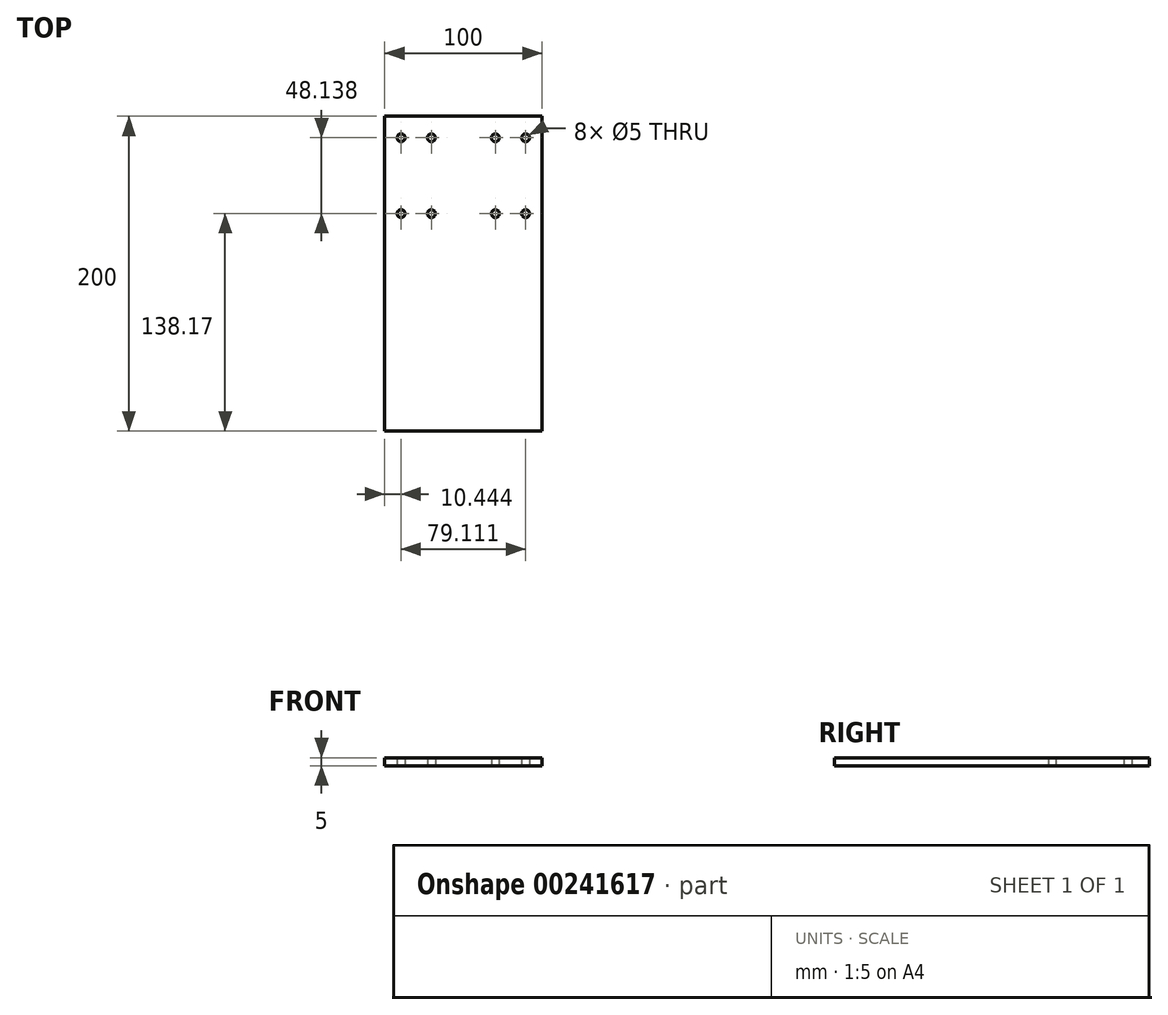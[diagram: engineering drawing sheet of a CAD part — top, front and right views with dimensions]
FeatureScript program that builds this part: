
annotation { "Feature Type Name" : "Feature", "Feature Type Description" : "" }
export const myFeature = defineFeature(function(context is Context, id is Id, definition is map)
    precondition{}
    {
        {
            var Q0;
            Q0=qCreatedBy(makeId("Top.planeOp"),FACE);
            var sketch = newSketch(context, id + "F0", { "sketchPlane" : qUnion([Q0])});
            skLineSegment(sketch, "E0.bottom", {"start": v(0, 0) * mm, "end": v(100, 0) * mm});
            skLineSegment(sketch, "E0.top", {"start": v(0, 200) * mm, "end": v(100, 200) * mm});
            skLineSegment(sketch, "E0.left", {"start": v(0, 0) * mm, "end": v(0, 200) * mm});
            skLineSegment(sketch, "E0.right", {"start": v(100, 0) * mm, "end": v(100, 200) * mm});
            skLineSegment(sketch, "E1", {"start": v(50, 200) * mm, "end": v(50, 0) * mm});
            skLineSegment(sketch, "E2.bottom", {"start": v(10.44, 186.3) * mm, "end": v(29.7, 186.3) * mm});
            skLineSegment(sketch, "E2.top", {"start": v(10.44, 138.17) * mm, "end": v(29.7, 138.17) * mm});
            skLineSegment(sketch, "E2.left", {"start": v(10.44, 186.3) * mm, "end": v(10.44, 138.17) * mm});
            skLineSegment(sketch, "E2.right", {"start": v(29.7, 186.3) * mm, "end": v(29.7, 138.17) * mm});
            skLineSegment(sketch, "E3.MirrorCS", {"start": v(89.56, 138.17) * mm, "end": v(70.3, 138.17) * mm});
            skLineSegment(sketch, "E4.MirrorCS", {"start": v(89.56, 186.3) * mm, "end": v(70.3, 186.3) * mm});
            skLineSegment(sketch, "E5.MirrorCS", {"start": v(70.3, 186.3) * mm, "end": v(70.3, 138.17) * mm});
            skLineSegment(sketch, "E6.MirrorCS", {"start": v(89.56, 186.3) * mm, "end": v(89.56, 138.17) * mm});
            skCircle(sketch, "E7", {"center": v(10.44, 186.3) * mm, "radius": 2.5 * mm});
            skCircle(sketch, "E8", {"center": v(29.7, 186.3) * mm, "radius": 2.5 * mm});
            skCircle(sketch, "E9", {"center": v(29.7, 138.17) * mm, "radius": 2.5 * mm});
            skCircle(sketch, "E10", {"center": v(10.44, 138.17) * mm, "radius": 2.5 * mm});
            skCircle(sketch, "E11", {"center": v(70.3, 186.3) * mm, "radius": 2.5 * mm});
            skCircle(sketch, "E12", {"center": v(89.56, 186.3) * mm, "radius": 2.5 * mm});
            skCircle(sketch, "E13", {"center": v(70.3, 138.17) * mm, "radius": 2.5 * mm});
            skCircle(sketch, "E14", {"center": v(89.56, 138.17) * mm, "radius": 2.5 * mm});
            skSolve(sketch);
        }
        {
            var Q0;
            {var subQ11=sQuery(id+"F0.wireOp",EDGE,"E0.right");Q0=makeQuery(id+"F0.imprint","IMPRINT",FACE,{"disambiguationData":[TD([[makeQuery(id+"F0.imprint","IMPRINT",EDGE,{"derivedFrom":subQ11}),1.0]])]});}
            var Q1;
            {var subQ10=sQuery(id+"F0.wireOp",EDGE,"E7");var subQ13=sQuery(id+"F0.wireOp",EDGE,"E2.bottom");var subQ14=makeQuery(id+"F0.imprint","INTERSECT",VERTEX,{"derivedFrom":[subQ13,subQ10]});Q1=makeQuery(id+"F0.imprint","IMPRINT",FACE,{"disambiguationData":[TD([[makeQuery(id+"F0.imprint","IMPRINT",EDGE,{"disambiguationData":[TD([[subQ14,-1.0]])],"derivedFrom":subQ13}),-1.0]])]});}
            var Q2;
            {var subQ15=sQuery(id+"F0.wireOp",EDGE,"E0.left");Q2=makeQuery(id+"F0.imprint","IMPRINT",FACE,{"disambiguationData":[TD([[makeQuery(id+"F0.imprint","IMPRINT",EDGE,{"derivedFrom":subQ15}),-1.0]])]});}
            var Q3;
            {var subQ3=sQuery(id+"F0.wireOp",EDGE,"E14");var subQ13=sQuery(id+"F0.wireOp",EDGE,"E3.MirrorCS");var subQ14=makeQuery(id+"F0.imprint","INTERSECT",VERTEX,{"derivedFrom":[subQ13,subQ3]});Q3=makeQuery(id+"F0.imprint","IMPRINT",FACE,{"disambiguationData":[TD([[makeQuery(id+"F0.imprint","IMPRINT",EDGE,{"disambiguationData":[TD([[subQ14,-1.0]])],"derivedFrom":subQ13}),-1.0]])]});}
            extrude(context, id + "F1", {"entities" : qUnion([Q0, Q1, Q2, Q3]), "depth" : 5 * mm});
        }
    });
